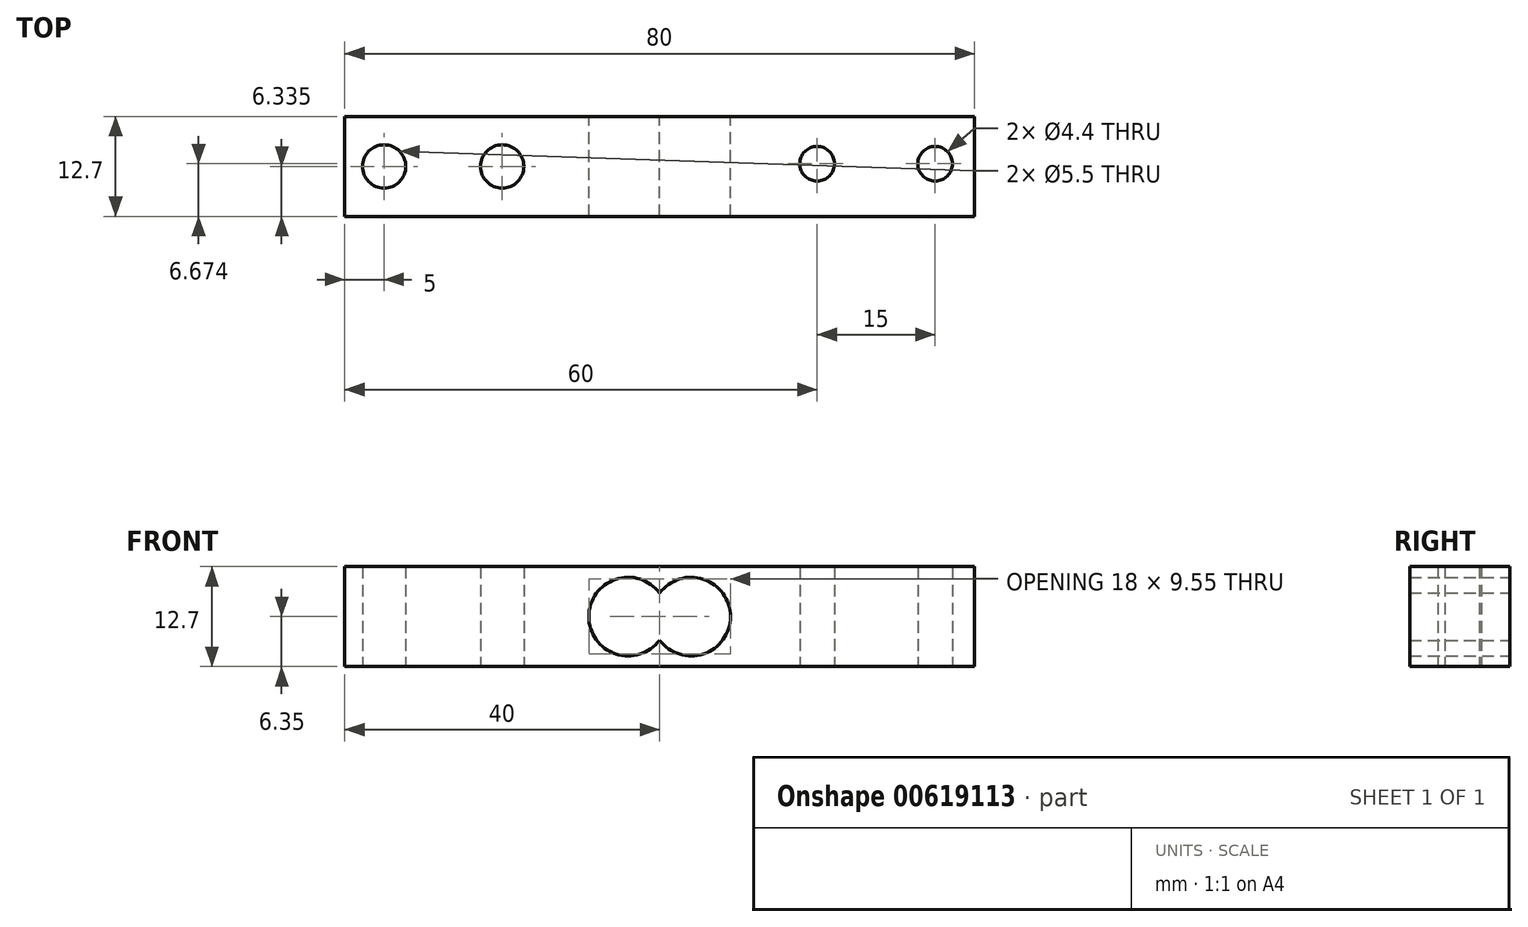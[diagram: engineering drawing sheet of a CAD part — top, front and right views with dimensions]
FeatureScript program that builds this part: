
annotation { "Feature Type Name" : "Feature", "Feature Type Description" : "" }
export const myFeature = defineFeature(function(context is Context, id is Id, definition is map)
    precondition{}
    {
        {
            var Q0;
            Q0=qCreatedBy(makeId("Front.planeOp"),FACE);
            var sketch = newSketch(context, id + "F0", { "sketchPlane" : qUnion([Q0])});
            skLineSegment(sketch, "E0.bottom", {"start": v(-40, 6.35) * mm, "end": v(40, 6.35) * mm});
            skLineSegment(sketch, "E0.top", {"start": v(-40, -6.35) * mm, "end": v(40, -6.35) * mm});
            skLineSegment(sketch, "E0.left", {"start": v(-40, 6.35) * mm, "end": v(-40, -6.35) * mm});
            skLineSegment(sketch, "E0.right", {"start": v(40, 6.35) * mm, "end": v(40, -6.35) * mm});
            skPoint(sketch, "E0.middle", {"position": v(0, 0) * mm});
            skSolve(sketch);
        }
        {
            var Q0;
            Q0 = qSketchRegion(id + "F0", true);
            extrude(context, id + "F1", {"entities" : qUnion([Q0]), "depth" : 12.7 * mm, "offsetDistance" : 25 * mm});
        }
        {
            var Q0;
            Q0=makeQuery(id+"F1.opExtrude","CAP_FACE",FACE,{"disambiguationData":[OSD([sQuery(id+"F0.wireOp",EDGE,"E0.bottom"),sQuery(id+"F0.wireOp",EDGE,"E0.top"),sQuery(id+"F0.wireOp",EDGE,"E0.left"),sQuery(id+"F0.wireOp",EDGE,"E0.right")])],"isStart":false});
            var sketch = newSketch(context, id + "F2", { "sketchPlane" : qUnion([Q0])});
            skPoint(sketch, "E1", {"position": v(-4, 0) * mm});
            skPoint(sketch, "E2", {"position": v(4, 0) * mm});
            skSolve(sketch);
        }
        {
            var Q0;
            Q0=sQuery(id+"F2.wireOp",VERTEX,"E1");
            var Q1;
            Q1=sQuery(id+"F2.wireOp",VERTEX,"E2");
            var Q2;
            Q2=makeQuery(id+"F1.opExtrude","SWEPT_BODY",BODY,{"disambiguationData":[OSD([sQuery(id+"F0.wireOp",EDGE,"E0.bottom"),sQuery(id+"F0.wireOp",EDGE,"E0.top"),sQuery(id+"F0.wireOp",EDGE,"E0.left"),sQuery(id+"F0.wireOp",EDGE,"E0.right")])]});
            hole(context, id + "F3", {"style" : HoleStyle.SIMPLE, "endStyle" : HoleEndStyle.THROUGH, "holeDiameter" : 10 * mm, "majorDiameter" : 5 * mm, "isTappedThrough" : true, "tappedDepth" : 12 * mm, "tapClearance" : 3, "locations" : qUnion([Q0, Q1]), "scope" : qUnion([Q2]), "startStyle" : HoleStartStyle.SKETCH});
        }
        {
            var Q0;
            Q0=makeQuery(id+"F1.opExtrude","SWEPT_FACE",FACE,{"disambiguationData":[OSD([sQuery(id+"F0.wireOp",EDGE,"E0.bottom")])]});
            var sketch = newSketch(context, id + "F4", { "sketchPlane" : qUnion([Q0])});
            skPoint(sketch, "E3", {"position": v(20, -6.03) * mm});
            skPoint(sketch, "E4", {"position": v(35, -6.03) * mm});
            skSolve(sketch);
        }
        {
            var Q0;
            Q0=sQuery(id+"F4.wireOp",VERTEX,"E3");
            var Q1;
            Q1=sQuery(id+"F4.wireOp",VERTEX,"E4");
            var Q2;
            Q2=makeQuery(id+"F1.opExtrude","SWEPT_BODY",BODY,{"disambiguationData":[OSD([sQuery(id+"F0.wireOp",EDGE,"E0.bottom"),sQuery(id+"F0.wireOp",EDGE,"E0.top"),sQuery(id+"F0.wireOp",EDGE,"E0.left"),sQuery(id+"F0.wireOp",EDGE,"E0.right")])]});
            hole(context, id + "F5", {"style" : HoleStyle.SIMPLE, "endStyle" : HoleEndStyle.THROUGH, "standardTappedOrClearance" : lookupTablePath({ "standard" : "ISO", "fit" : "Normal", "size" : "M4", "type" : "Clearance" }), "standardBlindInLast" : lookupTablePath({ "fit" : "Standard", "standard" : "ISO", "size" : "M4", "type" : "Clearance" }), "holeDiameter" : 4.4 * mm, "majorDiameter" : 5 * mm, "isTappedThrough" : true, "tappedDepth" : 12 * mm, "tapClearance" : 3, "locations" : qUnion([Q0, Q1]), "scope" : qUnion([Q2]), "startStyle" : HoleStartStyle.SKETCH});
        }
        {
            var Q0;
            Q0=makeQuery(id+"F1.opExtrude","SWEPT_FACE",FACE,{"disambiguationData":[OSD([sQuery(id+"F0.wireOp",EDGE,"E0.bottom")])]});
            var sketch = newSketch(context, id + "F6", { "sketchPlane" : qUnion([Q0])});
            skPoint(sketch, "E5", {"position": v(-20, -6.37) * mm});
            skPoint(sketch, "E6", {"position": v(-35, -6.37) * mm});
            skSolve(sketch);
        }
        {
            var Q0;
            Q0=sQuery(id+"F6.wireOp",VERTEX,"E6");
            var Q1;
            Q1=sQuery(id+"F6.wireOp",VERTEX,"E5");
            var Q2;
            Q2=makeQuery(id+"F1.opExtrude","SWEPT_BODY",BODY,{"disambiguationData":[OSD([sQuery(id+"F0.wireOp",EDGE,"E0.bottom"),sQuery(id+"F0.wireOp",EDGE,"E0.top"),sQuery(id+"F0.wireOp",EDGE,"E0.left"),sQuery(id+"F0.wireOp",EDGE,"E0.right")])]});
            hole(context, id + "F7", {"style" : HoleStyle.SIMPLE, "endStyle" : HoleEndStyle.THROUGH, "standardTappedOrClearance" : lookupTablePath({ "standard" : "ISO", "fit" : "Normal", "size" : "M5", "type" : "Clearance" }), "standardBlindInLast" : lookupTablePath({ "fit" : "Standard", "standard" : "ISO", "size" : "M5", "type" : "Clearance" }), "holeDiameter" : 5.5 * mm, "majorDiameter" : 5 * mm, "isTappedThrough" : true, "tappedDepth" : 12 * mm, "tapClearance" : 3, "locations" : qUnion([Q0, Q1]), "scope" : qUnion([Q2]), "startStyle" : HoleStartStyle.SKETCH});
        }
    });
